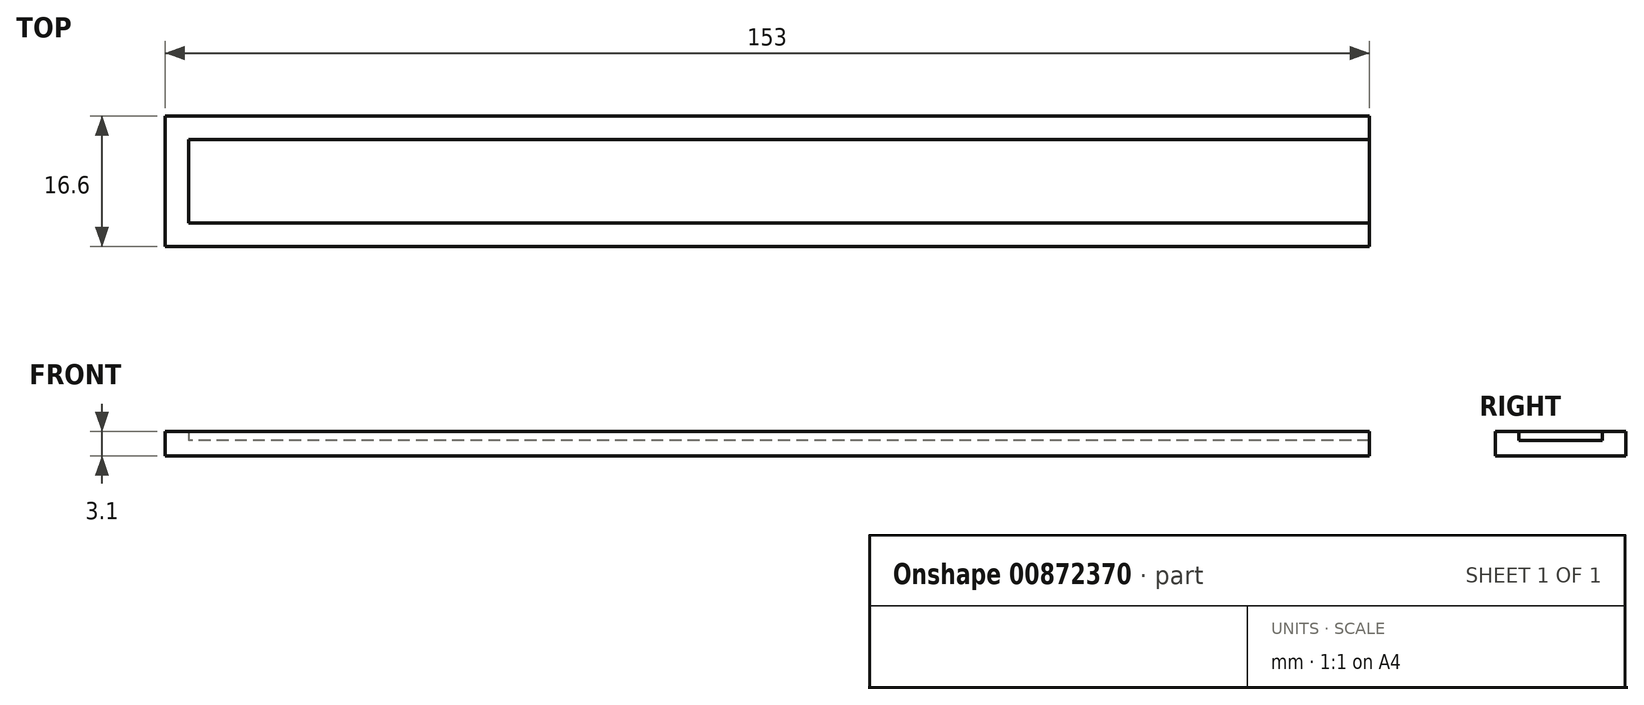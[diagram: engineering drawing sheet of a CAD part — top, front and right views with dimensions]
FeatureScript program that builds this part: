
annotation { "Feature Type Name" : "Feature", "Feature Type Description" : "" }
export const myFeature = defineFeature(function(context is Context, id is Id, definition is map)
    precondition{}
    {
        {
            var Q0;
            Q0=qCreatedBy(makeId("Top.planeOp"),FACE);
            var sketch = newSketch(context, id + "F0", { "sketchPlane" : qUnion([Q0])});
            skLineSegment(sketch, "E0.bottom", {"start": v(-75, 5.3) * mm, "end": v(75, 5.3) * mm});
            skLineSegment(sketch, "E0.top", {"start": v(-75, -5.3) * mm, "end": v(75, -5.3) * mm});
            skLineSegment(sketch, "E0.left", {"start": v(-75, 5.3) * mm, "end": v(-75, -5.3) * mm});
            skLineSegment(sketch, "E0.right", {"start": v(75, 5.3) * mm, "end": v(75, -5.3) * mm});
            skPoint(sketch, "E0.middle", {"position": v(0, 0) * mm});
            skLineSegment(sketch, "E1.top", {"start": v(-75, 8.3) * mm, "end": v(75, 8.3) * mm});
            skLineSegment(sketch, "E1.left", {"start": v(-75, 5.3) * mm, "end": v(-75, 8.3) * mm});
            skLineSegment(sketch, "E1.right", {"start": v(75, 5.3) * mm, "end": v(75, 8.3) * mm});
            skLineSegment(sketch, "E2.bottom", {"start": v(-75, 8.3) * mm, "end": v(-78, 8.3) * mm});
            skLineSegment(sketch, "E2.top", {"start": v(-75, -8.3) * mm, "end": v(-78, -8.3) * mm});
            skLineSegment(sketch, "E2.left", {"start": v(-75, 8.3) * mm, "end": v(-75, -8.3) * mm});
            skLineSegment(sketch, "E2.right", {"start": v(-78, 8.3) * mm, "end": v(-78, -8.3) * mm});
            skLineSegment(sketch, "E3.MirrorCS", {"start": v(-75, -8.3) * mm, "end": v(75, -8.3) * mm});
            skLineSegment(sketch, "E4.MirrorCS", {"start": v(-75, -8.3) * mm, "end": v(-75, 8.3) * mm});
            skLineSegment(sketch, "E5.MirrorCS", {"start": v(75, -5.3) * mm, "end": v(75, -8.3) * mm});
            skSolve(sketch);
        }
        {
            var Q0;
            Q0=makeQuery(id+"F0.imprint","IMPRINT",FACE,{"disambiguationData":[TD([[makeQuery(id+"F0.imprint","IMPRINT",EDGE,{"derivedFrom":sQuery(id+"F0.wireOp",EDGE,"E0.bottom")}),1.0]])]});
            var Q1;
            Q1=makeQuery(id+"F0.imprint","IMPRINT",FACE,{"disambiguationData":[TD([[makeQuery(id+"F0.imprint","IMPRINT",EDGE,{"derivedFrom":sQuery(id+"F0.wireOp",EDGE,"E0.bottom")}),-1.0]])]});
            var Q2;
            Q2=makeQuery(id+"F0.imprint","IMPRINT",FACE,{"disambiguationData":[TD([[makeQuery(id+"F0.imprint","IMPRINT",EDGE,{"derivedFrom":sQuery(id+"F0.wireOp",EDGE,"E0.left")}),-1.0]])]});
            var Q3;
            Q3=makeQuery(id+"F0.imprint","IMPRINT",FACE,{"disambiguationData":[TD([[makeQuery(id+"F0.imprint","IMPRINT",EDGE,{"derivedFrom":sQuery(id+"F0.wireOp",EDGE,"E0.top")}),-1.0]])]});
            extrude(context, id + "F1", {"entities" : qUnion([Q0, Q1, Q2, Q3]), "depth" : 2 * mm, "offsetDistance" : 25 * mm});
        }
        {
            var Q0;
            Q0=makeQuery(id+"F0.imprint","IMPRINT",FACE,{"disambiguationData":[TD([[makeQuery(id+"F0.imprint","IMPRINT",EDGE,{"derivedFrom":sQuery(id+"F0.wireOp",EDGE,"E0.bottom")}),1.0]])]});
            var Q1;
            Q1=makeQuery(id+"F0.imprint","IMPRINT",FACE,{"disambiguationData":[TD([[makeQuery(id+"F0.imprint","IMPRINT",EDGE,{"derivedFrom":sQuery(id+"F0.wireOp",EDGE,"E0.left")}),-1.0]])]});
            var Q2;
            Q2=makeQuery(id+"F0.imprint","IMPRINT",FACE,{"disambiguationData":[TD([[makeQuery(id+"F0.imprint","IMPRINT",EDGE,{"derivedFrom":sQuery(id+"F0.wireOp",EDGE,"E0.top")}),-1.0]])]});
            extrude(context, id + "F2", {"entities" : qUnion([Q0, Q1, Q2]), "operationType" : NewBodyOperationType.ADD, "depth" : 3.1 * mm, "offsetDistance" : 25 * mm});
        }
    });
